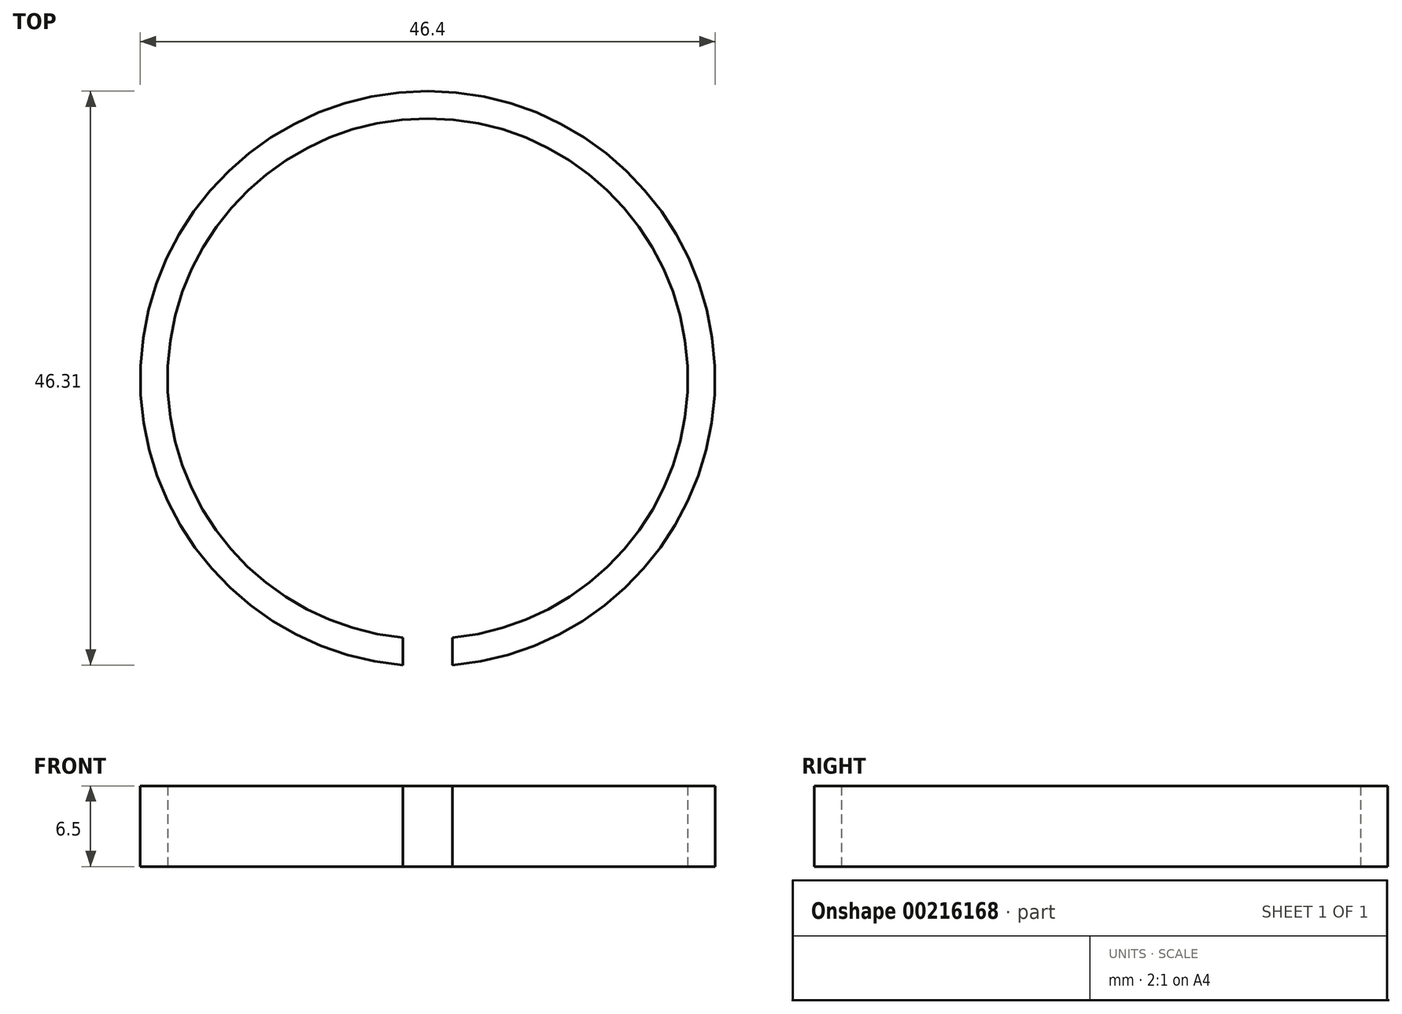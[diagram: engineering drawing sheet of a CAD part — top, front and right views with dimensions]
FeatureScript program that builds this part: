
annotation { "Feature Type Name" : "Feature", "Feature Type Description" : "" }
export const myFeature = defineFeature(function(context is Context, id is Id, definition is map)
    precondition{}
    {
        {
            var Q0;
            Q0=qCreatedBy(makeId("Top.planeOp"),FACE);
            var sketch = newSketch(context, id + "F0", { "sketchPlane" : qUnion([Q0])});
            skArc(sketch, "E0", {"start": v(2, -20.9) * mm, "mid": v(0, 21) * mm, "end": v(-2, -20.9) * mm});
            skArc(sketch, "E1", {"start": v(2, -23.11) * mm, "mid": v(0, 23.2) * mm, "end": v(-2, -23.11) * mm});
            skLineSegment(sketch, "E2.left", {"start": v(2, -23.11) * mm, "end": v(2, -20.9) * mm});
            skLineSegment(sketch, "E2.right", {"start": v(-2, -23.11) * mm, "end": v(-2, -20.9) * mm});
            skPoint(sketch, "E2.middle", {"position": v(0, -22) * mm});
            skSolve(sketch);
        }
        {
            var Q0;
            Q0 = qSketchRegion(id + "F0", true);
            extrude(context, id + "F1", {"entities" : qUnion([Q0]), "depth" : 6.5 * mm});
        }
    });
